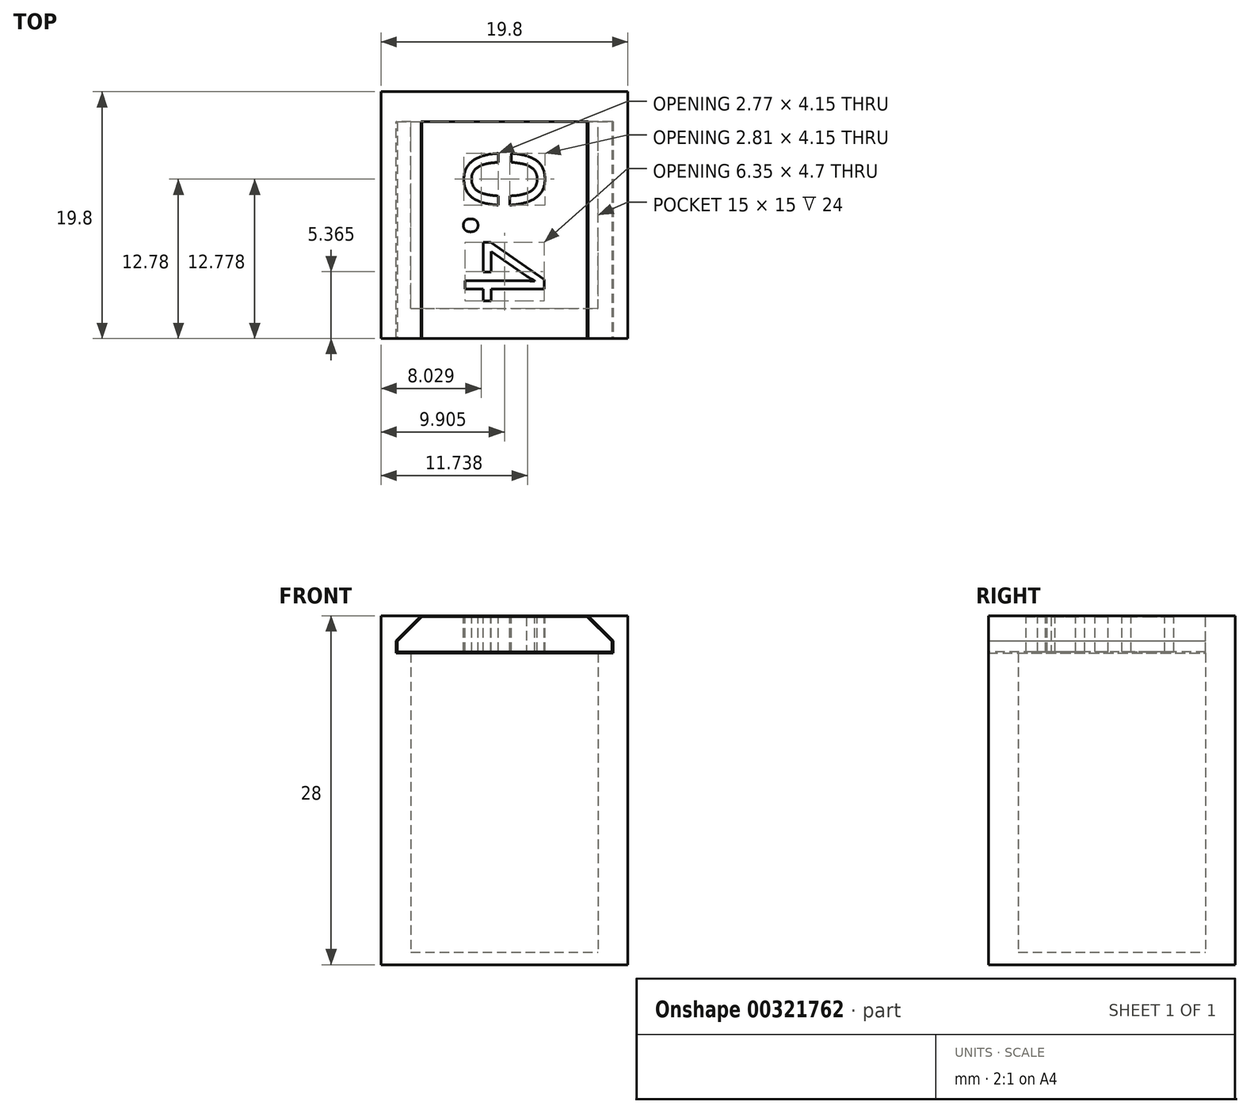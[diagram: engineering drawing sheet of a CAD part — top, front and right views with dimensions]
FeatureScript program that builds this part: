
annotation { "Feature Type Name" : "Feature", "Feature Type Description" : "" }
export const myFeature = defineFeature(function(context is Context, id is Id, definition is map)
    precondition{}
    {
        {
            var Q0;
            Q0=qCreatedBy(makeId("Top.planeOp"),FACE);
            var sketch = newSketch(context, id + "F0", { "sketchPlane" : qUnion([Q0])});
            skLineSegment(sketch, "E0.bottom", {"start": v(-7.5, -7.5) * mm, "end": v(7.5, -7.5) * mm});
            skLineSegment(sketch, "E0.top", {"start": v(-7.5, 7.5) * mm, "end": v(7.5, 7.5) * mm});
            skLineSegment(sketch, "E0.left", {"start": v(-7.5, -7.5) * mm, "end": v(-7.5, 7.5) * mm});
            skLineSegment(sketch, "E0.right", {"start": v(7.5, -7.5) * mm, "end": v(7.5, 7.5) * mm});
            skLineSegment(sketch, "E1", {"start": v(-7.5, 7.5) * mm, "end": v(-7.5, 9.9) * mm});
            skLineSegment(sketch, "E2", {"start": v(-7.5, 9.9) * mm, "end": v(-9.9, 9.9) * mm});
            skLineSegment(sketch, "E3", {"start": v(7.5, -7.5) * mm, "end": v(9.9, -7.5) * mm});
            skLineSegment(sketch, "E4", {"start": v(9.9, -7.5) * mm, "end": v(9.9, -9.9) * mm});
            skLineSegment(sketch, "E5", {"start": v(-7.5, 0) * mm, "end": v(0, 0) * mm});
            skLineSegment(sketch, "E6", {"start": v(0, 0) * mm, "end": v(0, -7.5) * mm});
            skLineSegment(sketch, "E7.bottom", {"start": v(-9.9, 9.9) * mm, "end": v(9.9, 9.9) * mm});
            skLineSegment(sketch, "E7.top", {"start": v(-9.9, -9.9) * mm, "end": v(9.9, -9.9) * mm});
            skLineSegment(sketch, "E7.left", {"start": v(-9.9, 9.9) * mm, "end": v(-9.9, -9.9) * mm});
            skLineSegment(sketch, "E7.right", {"start": v(9.9, 9.9) * mm, "end": v(9.9, -9.9) * mm});
            skSolve(sketch);
        }
        {
            var Q0;
            {var subQ0=sQuery(id+"F0.wireOp",EDGE,"E1");Q0=makeQuery(id+"F0.imprint","IMPRINT",FACE,{"disambiguationData":[TD([[makeQuery(id+"F0.imprint","IMPRINT",EDGE,{"derivedFrom":subQ0}),1.0]])]});}
            var Q1;
            Q1=makeQuery(id+"F0.imprint","IMPRINT",FACE,{"disambiguationData":[TD([[makeQuery(id+"F0.imprint","IMPRINT",EDGE,{"derivedFrom":sQuery(id+"F0.wireOp",EDGE,"E0.top")}),1.0]])]});
            extrude(context, id + "F1", {"entities" : qUnion([Q0, Q1]), "depth" : 25 * mm});
        }
        {
            var Q0;
            Q0=makeQuery(id+"F1.opExtrude","CAP_FACE",FACE,{"disambiguationData":[OSD([sQuery(id+"F0.wireOp",EDGE,"E0.bottom"),sQuery(id+"F0.wireOp",EDGE,"E0.top"),sQuery(id+"F0.wireOp",EDGE,"E0.left"),sQuery(id+"F0.wireOp",EDGE,"E0.right"),sQuery(id+"F0.wireOp",EDGE,"E7.bottom"),sQuery(id+"F0.wireOp",EDGE,"E7.top"),sQuery(id+"F0.wireOp",EDGE,"E7.left"),sQuery(id+"F0.wireOp",EDGE,"E7.right")])],"isStart":true});
            var sketch = newSketch(context, id + "F2", { "sketchPlane" : qUnion([Q0])});
            skLineSegment(sketch, "E8.bottom", {"start": v(-9.9, 9.9) * mm, "end": v(9.9, 9.9) * mm});
            skLineSegment(sketch, "E8.top", {"start": v(-9.9, -9.9) * mm, "end": v(9.9, -9.9) * mm});
            skLineSegment(sketch, "E8.left", {"start": v(-9.9, 9.9) * mm, "end": v(-9.9, -9.9) * mm});
            skLineSegment(sketch, "E8.right", {"start": v(9.9, 9.9) * mm, "end": v(9.9, -9.9) * mm});
            skSolve(sketch);
        }
        {
            var Q0;
            Q0=qSketchRegion(id+"F2",true);
            extrude(context, id + "F3", {"entities" : qUnion([Q0]), "operationType" : NewBodyOperationType.ADD, "depth" : 1 * mm});
        }
        {
            var Q0;
            Q0=makeQuery(id+"F1.opExtrude","CAP_FACE",FACE,{"disambiguationData":[OSD([sQuery(id+"F0.wireOp",EDGE,"E0.bottom"),sQuery(id+"F0.wireOp",EDGE,"E0.top"),sQuery(id+"F0.wireOp",EDGE,"E0.left"),sQuery(id+"F0.wireOp",EDGE,"E0.right"),sQuery(id+"F0.wireOp",EDGE,"E7.bottom"),sQuery(id+"F0.wireOp",EDGE,"E7.top"),sQuery(id+"F0.wireOp",EDGE,"E7.left"),sQuery(id+"F0.wireOp",EDGE,"E7.right")])],"isStart":false});
            var sketch = newSketch(context, id + "F4", { "sketchPlane" : qUnion([Q0])});
            skLineSegment(sketch, "E9", {"start": v(-9.9, 0) * mm, "end": v(-8.7, 0) * mm});
            skPoint(sketch, "E9.endSnap0", {"position": v(-7.5, 0) * mm});
            skLineSegment(sketch, "E10", {"start": v(9.9, 0) * mm, "end": v(8.7, 0) * mm});
            skLineSegment(sketch, "E11", {"start": v(-8.7, 0) * mm, "end": v(-8.7, -10.6) * mm});
            skLineSegment(sketch, "E12", {"start": v(8.7, 0) * mm, "end": v(8.7, -11.22) * mm});
            skLineSegment(sketch, "E13", {"start": v(-8.7, -10.6) * mm, "end": v(8.7, -10.6) * mm});
            skLineSegment(sketch, "E14", {"start": v(-7.5, 7.5) * mm, "end": v(-9.9, 7.5) * mm});
            skLineSegment(sketch, "E15", {"start": v(7.5, 7.5) * mm, "end": v(9.9, 7.5) * mm});
            skLineSegment(sketch, "E16", {"start": v(-8.7, 0) * mm, "end": v(-8.7, 7.5) * mm});
            skLineSegment(sketch, "E17", {"start": v(8.7, 0) * mm, "end": v(8.7, 7.5) * mm});
            skLineSegment(sketch, "E18", {"start": v(-7.5, 7.5) * mm, "end": v(7.5, 7.5) * mm});
            skSolve(sketch);
        }
        {
            var Q0;
            {var subQ11=sQuery(id+"F4.wireOp",EDGE,"E16");Q0=makeQuery(id+"F4.imprint","IMPRINT",FACE,{"disambiguationData":[TD([[makeQuery(id+"F4.imprint","IMPRINT",EDGE,{"derivedFrom":subQ11}),-1.0]])]});}
            extrude(context, id + "F5", {"entities" : qUnion([Q0]), "operationType" : NewBodyOperationType.REMOVE, "oppositeDirection" : true, "depth" : 2 * mm});
        }
        {
            var Q0;
            Q0=makeQuery(id+"F3.boolean.opBoolean","MERGE",FACE,{"derivedFrom":[makeQuery(id+"F1.opExtrude","SWEPT_FACE",FACE,{"disambiguationData":[OSD([sQuery(id+"F0.wireOp",EDGE,"E7.top")])]}),makeQuery(id+"F3.opExtrude","SWEPT_FACE",FACE,{"disambiguationData":[OSD([sQuery(id+"F2.wireOp",EDGE,"E8.bottom")])]})]});
            var sketch = newSketch(context, id + "F6", { "sketchPlane" : qUnion([Q0])});
            skLineSegment(sketch, "E19", {"start": v(-9.9, 25) * mm, "end": v(-9.9, 27) * mm});
            skLineSegment(sketch, "E20", {"start": v(9.9, 25) * mm, "end": v(9.9, 27) * mm});
            skLineSegment(sketch, "E21", {"start": v(-9.9, 27) * mm, "end": v(9.9, 27) * mm});
            skLineSegment(sketch, "E22", {"start": v(-8.7, 25) * mm, "end": v(-6.7, 27) * mm});
            skLineSegment(sketch, "E23", {"start": v(8.7, 25) * mm, "end": v(6.7, 27) * mm});
            skLineSegment(sketch, "E24", {"start": v(-9.9, 25) * mm, "end": v(-8.7, 25) * mm});
            skLineSegment(sketch, "E25", {"start": v(8.7, 25) * mm, "end": v(9.9, 25) * mm});
            skSolve(sketch);
        }
        {
            var Q0;
            Q0=makeQuery(id+"F5.boolean.opBoolean","COPY",FACE,{"derivedFrom":makeQuery(id+"F5.opExtrude","CAP_FACE",FACE,{"disambiguationData":[OSD([sQuery(id+"F0.wireOp",EDGE,"E0.bottom"),sQuery(id+"F0.wireOp",EDGE,"E0.left"),sQuery(id+"F0.wireOp",EDGE,"E0.right"),sQuery(id+"F0.wireOp",EDGE,"E7.top"),sQuery(id+"F4.wireOp",EDGE,"E11"),sQuery(id+"F4.wireOp",EDGE,"E12"),sQuery(id+"F4.wireOp",EDGE,"E14"),sQuery(id+"F4.wireOp",EDGE,"E15"),sQuery(id+"F4.wireOp",EDGE,"E16"),sQuery(id+"F4.wireOp",EDGE,"E17")])],"isStart":false})});
            extrude(context, id + "F7", {"entities" : qUnion([Q0]), "operationType" : NewBodyOperationType.ADD, "depth" : 1 * mm});
        }
        {
            var Q0;
            {var subQ0=sQuery(id+"F6.wireOp",EDGE,"E19");Q0=makeQuery(id+"F6.imprint","IMPRINT",FACE,{"disambiguationData":[TD([[makeQuery(id+"F6.imprint","IMPRINT",EDGE,{"derivedFrom":subQ0}),-1.0]])]});}
            var Q1;
            {var subQ0=sQuery(id+"F6.wireOp",EDGE,"E20");Q1=makeQuery(id+"F6.imprint","IMPRINT",FACE,{"disambiguationData":[TD([[makeQuery(id+"F6.imprint","IMPRINT",EDGE,{"derivedFrom":subQ0}),1.0]])]});}
            var Q2;
            Q2=makeQuery(id+"F3.boolean.opBoolean","MERGE",FACE,{"derivedFrom":[makeQuery(id+"F1.opExtrude","SWEPT_FACE",FACE,{"disambiguationData":[OSD([sQuery(id+"F0.wireOp",EDGE,"E7.bottom")])]}),makeQuery(id+"F3.opExtrude","SWEPT_FACE",FACE,{"disambiguationData":[OSD([sQuery(id+"F2.wireOp",EDGE,"E8.top")])]})]});
            extrude(context, id + "F8", {"entities" : qUnion([Q0, Q1]), "operationType" : NewBodyOperationType.ADD, "endBound" : BoundingType.UP_TO_SURFACE, "oppositeDirection" : true, "endBoundEntityFace" : qUnion([Q2]), "depth" : 25 * mm});
        }
        {
            var Q0;
            {var subQ0=sQuery(id+"F6.wireOp",EDGE,"E21");var subQ1=sQuery(id+"F2.wireOp",EDGE,"E8.top");var subQ2=sQuery(id+"F0.wireOp",EDGE,"E7.bottom");Q0=makeQuery(id+"F8.boolean.opBoolean","MERGE",FACE,{"derivedFrom":[makeQuery(id+"F3.boolean.opBoolean","MERGE",FACE,{"derivedFrom":[makeQuery(id+"F1.opExtrude","SWEPT_FACE",FACE,{"disambiguationData":[OSD([subQ2])]}),makeQuery(id+"F3.opExtrude","SWEPT_FACE",FACE,{"disambiguationData":[OSD([subQ1])]})]}),makeQuery(id+"F8.opExtrude","CAP_FACE",FACE,{"disambiguationData":[OSD([subQ2,subQ1]),ownerDisambiguation([makeQuery(id+"F8.opExtrude","SWEPT_BODY",BODY,{"disambiguationData":[OSD([sQuery(id+"F6.wireOp",EDGE,"E19"),subQ0,sQuery(id+"F6.wireOp",EDGE,"E22"),sQuery(id+"F6.wireOp",EDGE,"E24")])]})])],"isStart":false}),makeQuery(id+"F8.opExtrude","CAP_FACE",FACE,{"disambiguationData":[OSD([subQ2,subQ1]),ownerDisambiguation([makeQuery(id+"F8.opExtrude","SWEPT_BODY",BODY,{"disambiguationData":[OSD([sQuery(id+"F6.wireOp",EDGE,"E20"),subQ0,sQuery(id+"F6.wireOp",EDGE,"E23"),sQuery(id+"F6.wireOp",EDGE,"E25")])]})])],"isStart":false})]});}
            var sketch = newSketch(context, id + "F9", { "sketchPlane" : qUnion([Q0])});
            skLineSegment(sketch, "E26", {"start": v(-6.7, 27) * mm, "end": v(-6.7, 25) * mm});
            skLineSegment(sketch, "E27", {"start": v(-6.7, 25) * mm, "end": v(-8.7, 25) * mm});
            skLineSegment(sketch, "E28", {"start": v(-8.7, 25) * mm, "end": v(-6.7, 27) * mm});
            skLineSegment(sketch, "E29", {"start": v(6.7, 27) * mm, "end": v(6.7, 25) * mm});
            skLineSegment(sketch, "E30", {"start": v(6.7, 25) * mm, "end": v(8.7, 25) * mm});
            skLineSegment(sketch, "E31", {"start": v(8.7, 25) * mm, "end": v(6.7, 27) * mm});
            skSolve(sketch);
        }
        {
            var Q0;
            Q0=makeQuery(id+"F9.imprint","IMPRINT",FACE,{"disambiguationData":[TD([[makeQuery(id+"F9.imprint","IMPRINT",EDGE,{"derivedFrom":sQuery(id+"F9.wireOp",EDGE,"E26")}),-1.0]])]});
            var Q1;
            Q1=makeQuery(id+"F9.imprint","IMPRINT",FACE,{"disambiguationData":[TD([[makeQuery(id+"F9.imprint","IMPRINT",EDGE,{"derivedFrom":sQuery(id+"F9.wireOp",EDGE,"E29")}),1.0]])]});
            var Q2;
            Q2=makeQuery(id+"F5.boolean.opBoolean","MERGE",FACE,{"derivedFrom":[makeQuery(id+"F1.opExtrude","SWEPT_FACE",FACE,{"disambiguationData":[OSD([sQuery(id+"F0.wireOp",EDGE,"E0.top")])]}),makeQuery(id+"F5.opExtrude","SWEPT_FACE",FACE,{"disambiguationData":[OSD([sQuery(id+"F4.wireOp",EDGE,"E14")])]}),makeQuery(id+"F5.opExtrude","SWEPT_FACE",FACE,{"disambiguationData":[OSD([sQuery(id+"F4.wireOp",EDGE,"E15")])]})]});
            extrude(context, id + "F10", {"entities" : qUnion([Q0, Q1]), "operationType" : NewBodyOperationType.ADD, "endBound" : BoundingType.UP_TO_SURFACE, "oppositeDirection" : true, "endBoundEntityFace" : qUnion([Q2]), "depth" : 25 * mm});
        }
        {
            var Q0;
            Q0=makeQuery(id+"F1.opExtrude","CAP_FACE",FACE,{"disambiguationData":[OSD([sQuery(id+"F0.wireOp",EDGE,"E0.bottom"),sQuery(id+"F0.wireOp",EDGE,"E0.top"),sQuery(id+"F0.wireOp",EDGE,"E0.left"),sQuery(id+"F0.wireOp",EDGE,"E0.right"),sQuery(id+"F0.wireOp",EDGE,"E7.bottom"),sQuery(id+"F0.wireOp",EDGE,"E7.top"),sQuery(id+"F0.wireOp",EDGE,"E7.left"),sQuery(id+"F0.wireOp",EDGE,"E7.right")])],"isStart":false});
            var Q1;
            {var subQ0=sQuery(id+"F6.wireOp",EDGE,"E21");Q1=makeQuery(id+"F8.opExtrude","SWEPT_FACE",FACE,{"disambiguationData":[OSD([subQ0]),TDD([makeQuery(id+"F6.imprint","IMPRINT",EDGE,{"disambiguationData":[TD([[makeQuery(id+"F6.imprint","INTERSECT",VERTEX,{"derivedFrom":[sQuery(id+"F6.wireOp",EDGE,"E20"),subQ0]}),1.0]])],"derivedFrom":subQ0})])]});}
            extrude(context, id + "F11", {"entities" : qUnion([Q0]), "operationType" : NewBodyOperationType.ADD, "endBound" : BoundingType.UP_TO_SURFACE, "endBoundEntityFace" : qUnion([Q1]), "depth" : 25 * mm});
        }
        {
            var Q0;
            {var subQ0=sQuery(id+"F6.wireOp",EDGE,"E21");var subQ1=sQuery(id+"F0.wireOp",EDGE,"E7.top");Q0=makeQuery(id+"F8.boolean.opBoolean","MERGE",FACE,{"derivedFrom":[makeQuery(id+"F7.boolean.opBoolean","MERGE",FACE,{"derivedFrom":[makeQuery(id+"F3.boolean.opBoolean","MERGE",FACE,{"derivedFrom":[makeQuery(id+"F1.opExtrude","SWEPT_FACE",FACE,{"disambiguationData":[OSD([subQ1])]}),makeQuery(id+"F3.opExtrude","SWEPT_FACE",FACE,{"disambiguationData":[OSD([sQuery(id+"F2.wireOp",EDGE,"E8.bottom")])]})]}),makeQuery(id+"F7.opExtrude","SWEPT_FACE",FACE,{"disambiguationData":[OSD([subQ1])]})]}),makeQuery(id+"F8.opExtrude","CAP_FACE",FACE,{"disambiguationData":[OSD([sQuery(id+"F6.wireOp",EDGE,"E19"),subQ0,sQuery(id+"F6.wireOp",EDGE,"E22"),sQuery(id+"F6.wireOp",EDGE,"E24")])],"isStart":true}),makeQuery(id+"F8.opExtrude","CAP_FACE",FACE,{"disambiguationData":[OSD([sQuery(id+"F6.wireOp",EDGE,"E20"),subQ0,sQuery(id+"F6.wireOp",EDGE,"E23"),sQuery(id+"F6.wireOp",EDGE,"E25")])],"isStart":true})]});}
            var sketch = newSketch(context, id + "F12", { "sketchPlane" : qUnion([Q0])});
            skLineSegment(sketch, "E32.0", {"start": v(-8.6, 24.1) * mm, "end": v(-8.6, 24.96) * mm});
            skLineSegment(sketch, "E33.0", {"start": v(-8.6, 24.96) * mm, "end": v(-6.63, 26.93) * mm});
            skLineSegment(sketch, "E34.0", {"start": v(-8.6, 24.1) * mm, "end": v(8.6, 24.1) * mm});
            skLineSegment(sketch, "E35.0", {"start": v(8.6, 24.1) * mm, "end": v(8.6, 24.96) * mm});
            skLineSegment(sketch, "E36.0", {"start": v(8.6, 24.96) * mm, "end": v(6.63, 26.93) * mm});
            skLineSegment(sketch, "E37", {"start": v(-6.63, 26.93) * mm, "end": v(6.63, 26.93) * mm});
            skSolve(sketch);
        }
        {
            var Q0;
            Q0=makeQuery(id+"F12.imprint","IMPRINT",FACE,{"disambiguationData":[TD([[makeQuery(id+"F12.imprint","IMPRINT",EDGE,{"derivedFrom":sQuery(id+"F12.wireOp",EDGE,"E32.0")}),-1.0]])]});
            var Q1;
            {var subQ0=sQuery(id+"F4.wireOp",EDGE,"E15");var subQ1=sQuery(id+"F4.wireOp",EDGE,"E14");var subQ2=sQuery(id+"F0.wireOp",EDGE,"E0.top");Q1=makeQuery(id+"F11.boolean.opBoolean","MERGE",FACE,{"derivedFrom":[makeQuery(id+"F10.boolean.opBoolean","MERGE",FACE,{"derivedFrom":[makeQuery(id+"F5.boolean.opBoolean","MERGE",FACE,{"derivedFrom":[makeQuery(id+"F1.opExtrude","SWEPT_FACE",FACE,{"disambiguationData":[OSD([subQ2])]}),makeQuery(id+"F5.opExtrude","SWEPT_FACE",FACE,{"disambiguationData":[OSD([subQ1])]}),makeQuery(id+"F5.opExtrude","SWEPT_FACE",FACE,{"disambiguationData":[OSD([subQ0])]})]}),makeQuery(id+"F10.opExtrude","CAP_FACE",FACE,{"disambiguationData":[OSD([subQ2,subQ1,subQ0]),ownerDisambiguation([makeQuery(id+"F10.opExtrude","SWEPT_BODY",BODY,{"disambiguationData":[OSD([sQuery(id+"F9.wireOp",EDGE,"E26"),sQuery(id+"F9.wireOp",EDGE,"E27"),sQuery(id+"F9.wireOp",EDGE,"E28")])]})])],"isStart":false}),makeQuery(id+"F10.opExtrude","CAP_FACE",FACE,{"disambiguationData":[OSD([subQ2,subQ1,subQ0]),ownerDisambiguation([makeQuery(id+"F10.opExtrude","SWEPT_BODY",BODY,{"disambiguationData":[OSD([sQuery(id+"F9.wireOp",EDGE,"E29"),sQuery(id+"F9.wireOp",EDGE,"E30"),sQuery(id+"F9.wireOp",EDGE,"E31")])]})])],"isStart":false})]}),makeQuery(id+"F11.opExtrude","SWEPT_FACE",FACE,{"disambiguationData":[OSD([subQ2,subQ1,subQ0])]})]});}
            extrude(context, id + "F13", {"entities" : qUnion([Q0]), "endBound" : BoundingType.UP_TO_SURFACE, "oppositeDirection" : true, "endBoundEntityFace" : qUnion([Q1]), "depth" : 25 * mm});
        }
        {
            var Q0;
            Q0=makeQuery(id+"F13.opExtrude","SWEPT_FACE",FACE,{"disambiguationData":[OSD([sQuery(id+"F12.wireOp",EDGE,"E37")])]});
            var sketch = newSketch(context, id + "F14", { "sketchPlane" : qUnion([Q0])});
            skText(sketch, "E38", { "text": "0.4", "fontName": "OpenSans-Regular.ttf"});
            const initialGuessF14  = {"E38": [-0.00317, 0.00541, 0, -1, 0.00637]};
            skSetInitialGuess(sketch, initialGuessF14);
            skSolve(sketch);
        }
        {
            var Q0;
            Q0 = qSketchRegion(id + "F14", true);
            extrude(context, id + "F15", {"entities" : qUnion([Q0]), "operationType" : NewBodyOperationType.REMOVE, "oppositeDirection" : true, "depth" : 2 * mm});
        }
        {
            var Q0;
            Q0=makeQuery(id+"F15.boolean.opBoolean","COPY",FACE,{"derivedFrom":makeQuery(id+"F15.opExtrude","CAP_FACE",FACE,{"disambiguationData":[OSD([sQuery(id+"F14.wireOp",EDGE,"E38.sketch_text.stroke-0"),sQuery(id+"F14.wireOp",EDGE,"E38.sketch_text.stroke-1"),sQuery(id+"F14.wireOp",EDGE,"E38.sketch_text.stroke-2"),sQuery(id+"F14.wireOp",EDGE,"E38.sketch_text.stroke-3"),sQuery(id+"F14.wireOp",EDGE,"E38.sketch_text.stroke-4"),sQuery(id+"F14.wireOp",EDGE,"E38.sketch_text.stroke-5"),sQuery(id+"F14.wireOp",EDGE,"E38.sketch_text.stroke-6"),sQuery(id+"F14.wireOp",EDGE,"E38.sketch_text.stroke-7"),sQuery(id+"F14.wireOp",EDGE,"E38.sketch_text.stroke-8"),sQuery(id+"F14.wireOp",EDGE,"E38.sketch_text.stroke-9"),sQuery(id+"F14.wireOp",EDGE,"E38.sketch_text.stroke-10"),sQuery(id+"F14.wireOp",EDGE,"E38.sketch_text.stroke-11"),sQuery(id+"F14.wireOp",EDGE,"E38.sketch_text.stroke-12"),sQuery(id+"F14.wireOp",EDGE,"E38.sketch_text.stroke-13"),sQuery(id+"F14.wireOp",EDGE,"E38.sketch_text.stroke-14"),sQuery(id+"F14.wireOp",EDGE,"E38.sketch_text.stroke-15")])],"isStart":false})});
            var Q1;
            Q1=makeQuery(id+"F15.boolean.opBoolean","COPY",FACE,{"derivedFrom":makeQuery(id+"F15.opExtrude","CAP_FACE",FACE,{"disambiguationData":[OSD([sQuery(id+"F14.wireOp",EDGE,"E38.sketch_text.stroke-16"),sQuery(id+"F14.wireOp",EDGE,"E38.sketch_text.stroke-17"),sQuery(id+"F14.wireOp",EDGE,"E38.sketch_text.stroke-18"),sQuery(id+"F14.wireOp",EDGE,"E38.sketch_text.stroke-19"),sQuery(id+"F14.wireOp",EDGE,"E38.sketch_text.stroke-20"),sQuery(id+"F14.wireOp",EDGE,"E38.sketch_text.stroke-21"),sQuery(id+"F14.wireOp",EDGE,"E38.sketch_text.stroke-22"),sQuery(id+"F14.wireOp",EDGE,"E38.sketch_text.stroke-23")])],"isStart":false})});
            var Q2;
            Q2=makeQuery(id+"F15.boolean.opBoolean","COPY",FACE,{"derivedFrom":makeQuery(id+"F15.opExtrude","CAP_FACE",FACE,{"disambiguationData":[OSD([sQuery(id+"F14.wireOp",EDGE,"E38.sketch_text.stroke-24"),sQuery(id+"F14.wireOp",EDGE,"E38.sketch_text.stroke-25"),sQuery(id+"F14.wireOp",EDGE,"E38.sketch_text.stroke-26"),sQuery(id+"F14.wireOp",EDGE,"E38.sketch_text.stroke-27"),sQuery(id+"F14.wireOp",EDGE,"E38.sketch_text.stroke-28"),sQuery(id+"F14.wireOp",EDGE,"E38.sketch_text.stroke-29"),sQuery(id+"F14.wireOp",EDGE,"E38.sketch_text.stroke-30"),sQuery(id+"F14.wireOp",EDGE,"E38.sketch_text.stroke-31"),sQuery(id+"F14.wireOp",EDGE,"E38.sketch_text.stroke-32"),sQuery(id+"F14.wireOp",EDGE,"E38.sketch_text.stroke-33"),sQuery(id+"F14.wireOp",EDGE,"E38.sketch_text.stroke-34"),sQuery(id+"F14.wireOp",EDGE,"E38.sketch_text.stroke-35"),sQuery(id+"F14.wireOp",EDGE,"E38.sketch_text.stroke-36"),sQuery(id+"F14.wireOp",EDGE,"E38.sketch_text.stroke-37"),sQuery(id+"F14.wireOp",EDGE,"E38.sketch_text.stroke-38"),sQuery(id+"F14.wireOp",EDGE,"E38.sketch_text.stroke-39"),sQuery(id+"F14.wireOp",EDGE,"E38.sketch_text.stroke-40")])],"isStart":false})});
            extrude(context, id + "F16", {"entities" : qUnion([Q0, Q1, Q2]), "operationType" : NewBodyOperationType.REMOVE, "oppositeDirection" : true, "depth" : 2 * mm});
        }
        {
            var Q0;
            {var subQ1=sQuery(id+"F12.wireOp",EDGE,"E33.0");var subQ2=sQuery(id+"F12.wireOp",EDGE,"E37");Q0=makeQuery(id+"F15.boolean.opBoolean","SPLIT",FACE,{"disambiguationData":[TD([makeQuery(id+"F13.opExtrude","SWEPT_FACE",FACE,{"disambiguationData":[OSD([subQ1])]})])],"derivedFrom":makeQuery(id+"F13.opExtrude","SWEPT_FACE",FACE,{"disambiguationData":[OSD([subQ2])]})});}
            var sketch = newSketch(context, id + "F17", { "sketchPlane" : qUnion([Q0])});
            skLineSegment(sketch, "E39", {"start": v(0, 4.97) * mm, "end": v(0, 4) * mm});
            skLineSegment(sketch, "E40", {"start": v(0, 4) * mm, "end": v(-0.49, 4) * mm});
            skLineSegment(sketch, "E41", {"start": v(-0.49, 4) * mm, "end": v(-0.49, 5.29) * mm});
            skLineSegment(sketch, "E42", {"start": v(-0.49, 5.29) * mm, "end": v(0.54, 5.29) * mm});
            skLineSegment(sketch, "E43", {"start": v(0.54, 5.29) * mm, "end": v(0.54, 4) * mm});
            skLineSegment(sketch, "E44", {"start": v(0.54, 4) * mm, "end": v(0, 4) * mm});
            skLineSegment(sketch, "E45", {"start": v(-0.49, 1.88) * mm, "end": v(0.43, 1.88) * mm});
            skLineSegment(sketch, "E46", {"start": v(0.43, 1.88) * mm, "end": v(0.43, 0.38) * mm});
            skLineSegment(sketch, "E47", {"start": v(0.43, 0.38) * mm, "end": v(-0.49, 0.38) * mm});
            skLineSegment(sketch, "E48", {"start": v(-0.49, 0.38) * mm, "end": v(-0.49, 1.88) * mm});
            skLineSegment(sketch, "E49", {"start": v(-1.72, -5.25) * mm, "end": v(-0.8, -5.25) * mm});
            skLineSegment(sketch, "E50", {"start": v(-0.8, -5.25) * mm, "end": v(-0.8, -4.57) * mm});
            skLineSegment(sketch, "E51", {"start": v(-0.8, -4.57) * mm, "end": v(-2.2, -4.57) * mm});
            skLineSegment(sketch, "E52", {"start": v(-2.2, -4.57) * mm, "end": v(-1.72, -5.25) * mm});
            skSolve(sketch);
        }
        {
            var Q0;
            {var subQ0=sQuery(id+"F17.wireOp",EDGE,"E39");Q0=makeQuery(id+"F17.imprint","IMPRINT",FACE,{"disambiguationData":[TD([[makeQuery(id+"F17.imprint","IMPRINT",EDGE,{"derivedFrom":subQ0}),-1.0]])]});}
            var Q1;
            {var subQ0=sQuery(id+"F17.wireOp",EDGE,"E39");Q1=makeQuery(id+"F17.imprint","IMPRINT",FACE,{"disambiguationData":[TD([[makeQuery(id+"F17.imprint","IMPRINT",EDGE,{"derivedFrom":subQ0}),1.0]])]});}
            var Q2;
            {var subQ6=sQuery(id+"F17.wireOp",EDGE,"E45");Q2=makeQuery(id+"F17.imprint","IMPRINT",FACE,{"disambiguationData":[TD([[makeQuery(id+"F17.imprint","IMPRINT",EDGE,{"derivedFrom":subQ6}),-1.0]])]});}
            var Q3;
            {var subQ0=sQuery(id+"F17.wireOp",EDGE,"E49");Q3=makeQuery(id+"F17.imprint","IMPRINT",FACE,{"disambiguationData":[TD([[makeQuery(id+"F17.imprint","IMPRINT",EDGE,{"derivedFrom":subQ0}),1.0]])]});}
            var Q4;
            {var subQ27=sQuery(id+"F12.wireOp",EDGE,"E32.0");var subQ29=sQuery(id+"F12.wireOp",EDGE,"E34.0");Q4=makeQuery(id+"F16.boolean.opBoolean","SPLIT",FACE,{"disambiguationData":[TD([makeQuery(id+"F13.opExtrude","SWEPT_FACE",FACE,{"disambiguationData":[OSD([subQ27])]})])],"derivedFrom":makeQuery(id+"F13.opExtrude","SWEPT_FACE",FACE,{"disambiguationData":[OSD([subQ29])]})});}
            extrude(context, id + "F18", {"entities" : qUnion([Q0, Q1, Q2, Q3]), "operationType" : NewBodyOperationType.ADD, "endBound" : BoundingType.UP_TO_SURFACE, "oppositeDirection" : true, "endBoundEntityFace" : qUnion([Q4]), "depth" : 3 * mm});
        }
    });
